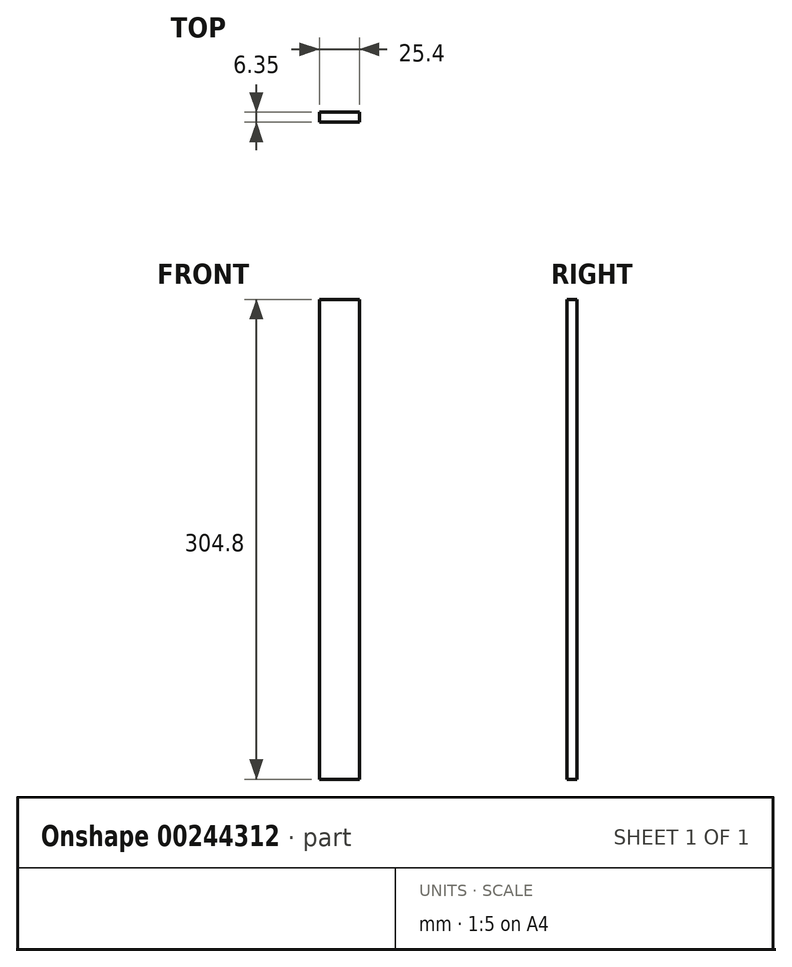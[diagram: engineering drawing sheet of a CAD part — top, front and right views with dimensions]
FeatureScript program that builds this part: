
annotation { "Feature Type Name" : "Feature", "Feature Type Description" : "" }
export const myFeature = defineFeature(function(context is Context, id is Id, definition is map)
    precondition{}
    {
        {
            var Q0;
            Q0=qCreatedBy(makeId("Front.planeOp"),FACE);
            var sketch = newSketch(context, id + "F0", { "sketchPlane" : qUnion([Q0])});
            skLineSegment(sketch, "E0.bottom", {"start": v(-11.7, 192.75) * mm, "end": v(13.7, 192.75) * mm});
            skLineSegment(sketch, "E0.top", {"start": v(-11.7, -112.05) * mm, "end": v(13.7, -112.05) * mm});
            skLineSegment(sketch, "E0.left", {"start": v(-11.7, 192.75) * mm, "end": v(-11.7, -112.05) * mm});
            skLineSegment(sketch, "E0.right", {"start": v(13.7, 192.75) * mm, "end": v(13.7, -112.05) * mm});
            skSolve(sketch);
        }
        {
            var Q0;
            Q0=makeQuery(id+"F0.imprint","IMPRINT",FACE,{"disambiguationData":[TD([[makeQuery(id+"F0.imprint","IMPRINT",EDGE,{"derivedFrom":sQuery(id+"F0.wireOp",EDGE,"E0.bottom")}),-1.0]])]});
            extrude(context, id + "F1", {"entities" : qUnion([Q0]), "depth" : 6.35 * mm});
        }
    });
